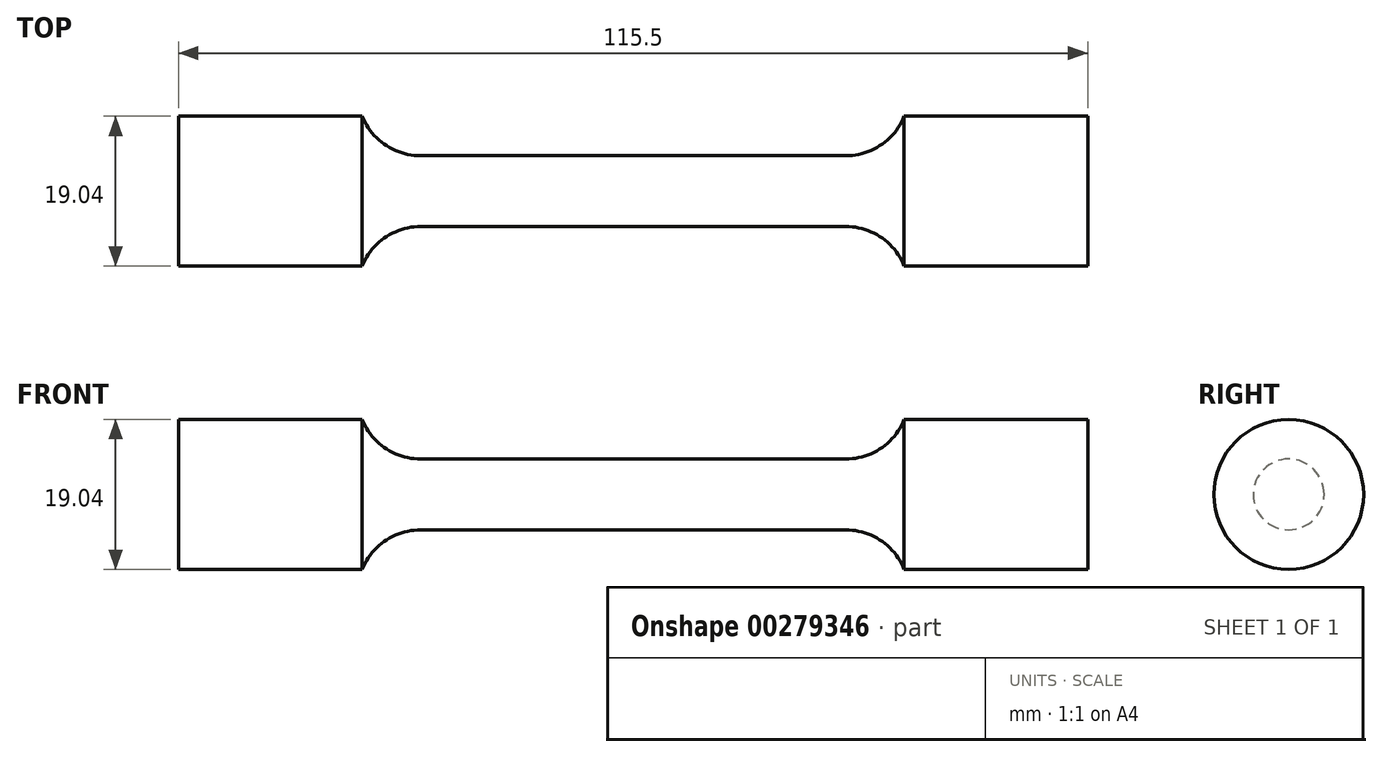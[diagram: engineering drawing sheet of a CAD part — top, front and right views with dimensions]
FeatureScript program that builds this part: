
annotation { "Feature Type Name" : "Feature", "Feature Type Description" : "" }
export const myFeature = defineFeature(function(context is Context, id is Id, definition is map)
    precondition{}
    {
        {
            var Q0;
            Q0=qCreatedBy(makeId("Front.planeOp"),FACE);
            var sketch = newSketch(context, id + "F0", { "sketchPlane" : qUnion([Q0])});
            skLineSegment(sketch, "E0", {"start": v(0, 4.5) * mm, "end": v(27, 4.5) * mm});
            skArc(sketch, "E1", {"start": v(27, 4.5) * mm, "mid": v(31.48, 5.87) * mm, "end": v(34.42, 9.52) * mm});
            skLineSegment(sketch, "E2", {"start": v(34.42, 9.52) * mm, "end": v(57.75, 9.52) * mm});
            skLineSegment(sketch, "E3", {"start": v(57.75, 9.52) * mm, "end": v(57.75, 0) * mm});
            skLineSegment(sketch, "E4.MirrorCS", {"start": v(0, 4.5) * mm, "end": v(-27, 4.5) * mm});
            skLineSegment(sketch, "E5.MirrorCS", {"start": v(-57.75, 9.52) * mm, "end": v(-57.75, 0) * mm});
            skLineSegment(sketch, "E6.MirrorCS", {"start": v(-34.42, 9.52) * mm, "end": v(-57.75, 9.52) * mm});
            skArc(sketch, "E7.MirrorCS", {"start": v(-27, 4.5) * mm, "mid": v(-31.48, 5.87) * mm, "end": v(-34.42, 9.52) * mm});
            skLineSegment(sketch, "E8", {"start": v(-57.75, 0) * mm, "end": v(57.75, 0) * mm});
            skSolve(sketch);
        }
        {
            var Q0;
            Q0 = qSketchRegion(id + "F0", true);
            var Q1;
            Q1=sQuery(id+"F0.wireOp",EDGE,"E8");
            revolve(context, id + "F1", {"entities" : qUnion([Q0]), "axis" : qUnion([Q1]), "revolveType" : RevolveType.FULL});
        }
    });
